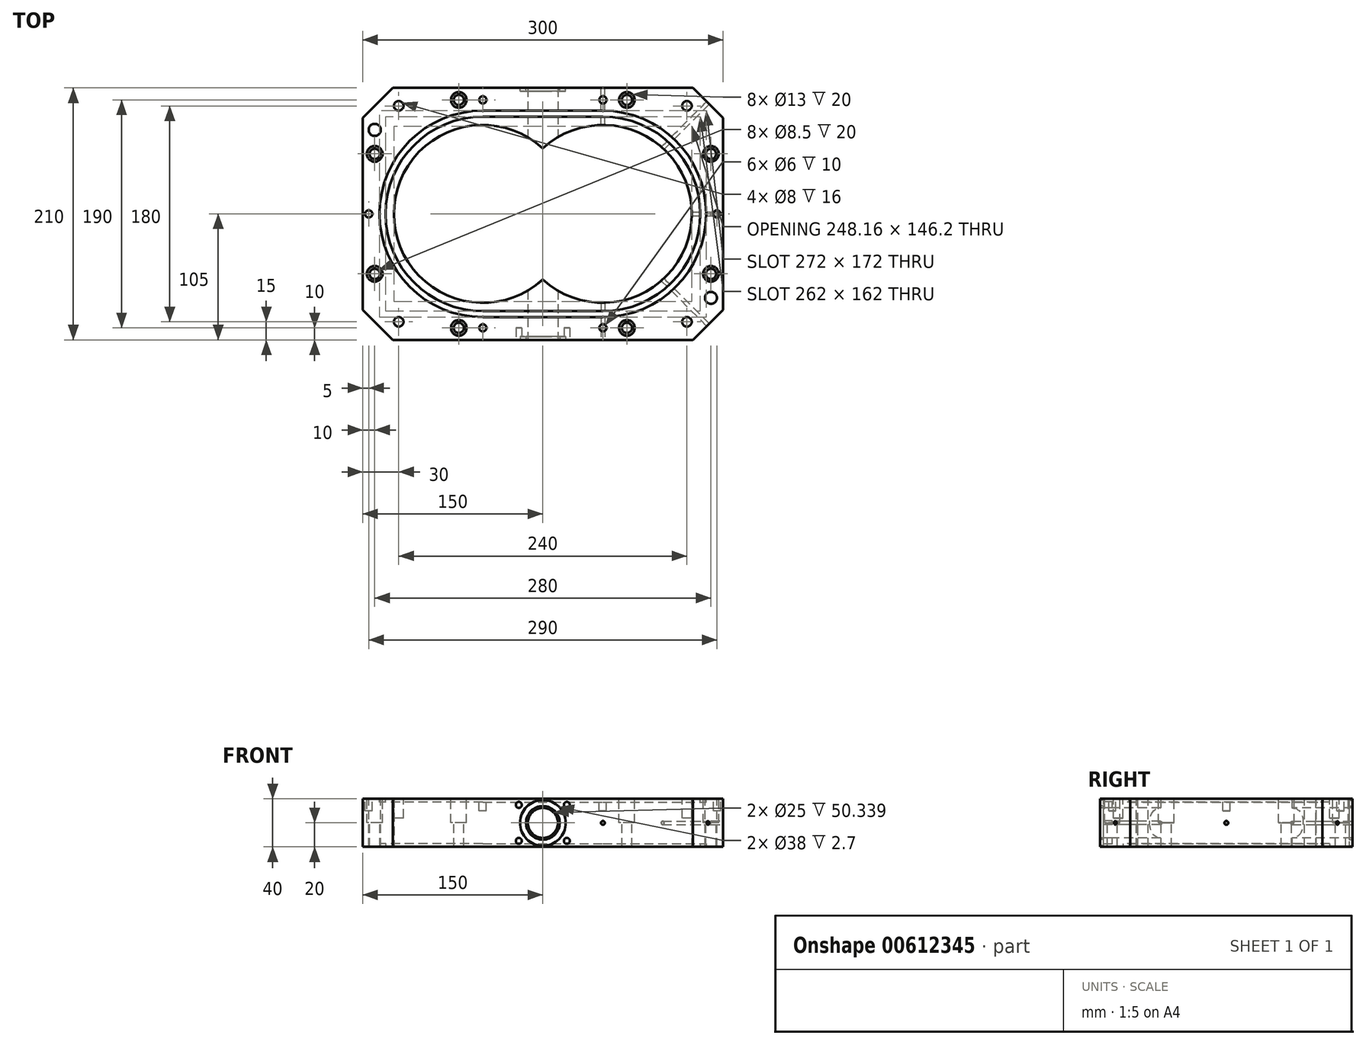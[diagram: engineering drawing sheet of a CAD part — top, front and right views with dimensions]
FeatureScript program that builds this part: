
annotation { "Feature Type Name" : "Feature", "Feature Type Description" : "" }
export const myFeature = defineFeature(function(context is Context, id is Id, definition is map)
    precondition{}
    {
        {
            var Q0;
            Q0=qCreatedBy(makeId("Top.planeOp"),FACE);
            var sketch = newSketch(context, id + "F0", { "sketchPlane" : qUnion([Q0])});
            skLineSegment(sketch, "E0.top", {"start": v(-150, 105) * mm, "end": v(150, 105) * mm});
            skLineSegment(sketch, "E0.right", {"start": v(150, -105) * mm, "end": v(150, 105) * mm});
            skArc(sketch, "E1", {"start": v(-50, 81) * mm, "mid": v(-131, 0) * mm, "end": v(-50, -81) * mm});
            skArc(sketch, "E2", {"start": v(50, -81) * mm, "mid": v(131, 0) * mm, "end": v(50, 81) * mm});
            skArc(sketch, "E3", {"start": v(-50, 86) * mm, "mid": v(-136, 0) * mm, "end": v(-50, -86) * mm});
            skArc(sketch, "E4", {"start": v(0, 54.66) * mm, "mid": v(-124.08, 0) * mm, "end": v(0, -54.66) * mm});
            skArc(sketch, "E5", {"start": v(50, -86) * mm, "mid": v(136, 0) * mm, "end": v(50, 86) * mm});
            skArc(sketch, "E6", {"start": v(0, -54.66) * mm, "mid": v(124.08, 0) * mm, "end": v(0, 54.66) * mm});
            skLineSegment(sketch, "E7", {"start": v(-50, -81) * mm, "end": v(50, -81) * mm});
            skLineSegment(sketch, "E8", {"start": v(-50, 81) * mm, "end": v(50, 81) * mm});
            skLineSegment(sketch, "E9", {"start": v(-50, 86) * mm, "end": v(50, 86) * mm});
            skLineSegment(sketch, "E10", {"start": v(50, -86) * mm, "end": v(-50, -86) * mm});
            skLineSegment(sketch, "E11", {"start": v(-150, 105) * mm, "end": v(-150, -105) * mm});
            skLineSegment(sketch, "E12", {"start": v(-150, -105) * mm, "end": v(150, -105) * mm});
            skSolve(sketch);
        }
        {
            var Q0;
            Q0=makeQuery(id+"F0.imprint","IMPRINT",FACE,{"disambiguationData":[TD([[makeQuery(id+"F0.imprint","IMPRINT",EDGE,{"derivedFrom":sQuery(id+"F0.wireOp",EDGE,"E0.top")}),-1.0]])]});
            var Q1;
            Q1=makeQuery(id+"F0.imprint","IMPRINT",FACE,{"disambiguationData":[TD([[makeQuery(id+"F0.imprint","IMPRINT",EDGE,{"derivedFrom":sQuery(id+"F0.wireOp",EDGE,"E1")}),-1.0]])]});
            var Q2;
            Q2=makeQuery(id+"F0.imprint","IMPRINT",FACE,{"disambiguationData":[TD([[makeQuery(id+"F0.imprint","IMPRINT",EDGE,{"derivedFrom":sQuery(id+"F0.wireOp",EDGE,"E1")}),1.0]])]});
            extrude(context, id + "F1", {"entities" : qUnion([Q0, Q1, Q2]), "depth" : 20 * mm, "offsetDistance" : 25 * mm, "hasSecondDirection" : true, "secondDirectionOppositeDirection" : true, "secondDirectionDepth" : 20 * mm});
        }
        {
            var Q0;
            Q0=qCreatedBy(makeId("Front.planeOp"),FACE);
            var sketch = newSketch(context, id + "F2", { "sketchPlane" : qUnion([Q0])});
            skCircle(sketch, "E13", {"center": v(0, 0) * mm, "radius": 12.5 * mm});
            skSolve(sketch);
        }
        {
            var Q0;
            Q0=makeQuery(id+"F2.imprint","IMPRINT",FACE,{"disambiguationData":[TD([[makeQuery(id+"F2.imprint","IMPRINT",EDGE,{"derivedFrom":sQuery(id+"F2.wireOp",EDGE,"E13")}),1.0]])]});
            extrude(context, id + "F3", {"entities" : qUnion([Q0]), "operationType" : NewBodyOperationType.REMOVE, "oppositeDirection" : true, "depth" : 105 * mm, "offsetDistance" : 25 * mm, "hasSecondDirection" : true, "secondDirectionOppositeDirection" : false, "secondDirectionDepth" : 105 * mm});
        }
        {
            var Q0;
            Q0=makeQuery(id+"F1.opExtrude","SWEPT_FACE",FACE,{"disambiguationData":[OSD([sQuery(id+"F0.wireOp",EDGE,"E12")])]});
            var sketch = newSketch(context, id + "F4", { "sketchPlane" : qUnion([Q0])});
            skCircle(sketch, "E14", {"center": v(0, 0) * mm, "radius": 19 * mm});
            skCircle(sketch, "E15", {"center": v(0, 0) * mm, "radius": 14 * mm});
            skCircle(sketch, "E16", {"center": v(50, 0) * mm, "radius": 1.59 * mm});
            skCircle(sketch, "E17", {"center": v(50, 0) * mm, "radius": 1.5 * mm});
            skCircle(sketch, "E18", {"center": v(-20, 15) * mm, "radius": 2.5 * mm});
            skCircle(sketch, "E19", {"center": v(-20, -15) * mm, "radius": 2.5 * mm});
            skCircle(sketch, "E20", {"center": v(20, -15) * mm, "radius": 2.5 * mm});
            skCircle(sketch, "E21", {"center": v(20, 15) * mm, "radius": 2.5 * mm});
            skSolve(sketch);
        }
        {
            var Q0;
            Q0=makeQuery(id+"F4.imprint","IMPRINT",FACE,{"disambiguationData":[TD([[makeQuery(id+"F4.imprint","IMPRINT",EDGE,{"derivedFrom":sQuery(id+"F4.wireOp",EDGE,"E14")}),1.0]])]});
            extrude(context, id + "F5", {"entities" : qUnion([Q0]), "operationType" : NewBodyOperationType.REMOVE, "oppositeDirection" : true, "depth" : 2.7 * mm, "offsetDistance" : 25 * mm});
        }
        {
            var Q0;
            Q0=makeQuery(id+"F1.opExtrude","SWEPT_FACE",FACE,{"disambiguationData":[OSD([sQuery(id+"F0.wireOp",EDGE,"E0.top")])]});
            var sketch = newSketch(context, id + "F6", { "sketchPlane" : qUnion([Q0])});
            skCircle(sketch, "E22", {"center": v(0, 0) * mm, "radius": 19 * mm});
            skCircle(sketch, "E23", {"center": v(0, 0) * mm, "radius": 14 * mm});
            skCircle(sketch, "E24", {"center": v(-50, 0) * mm, "radius": 1.59 * mm});
            skCircle(sketch, "E25", {"center": v(-50, 0) * mm, "radius": 1.5 * mm});
            skSolve(sketch);
        }
        {
            var Q0;
            Q0=makeQuery(id+"F6.imprint","IMPRINT",FACE,{"disambiguationData":[TD([[makeQuery(id+"F6.imprint","IMPRINT",EDGE,{"derivedFrom":sQuery(id+"F6.wireOp",EDGE,"E22")}),1.0]])]});
            extrude(context, id + "F7", {"entities" : qUnion([Q0]), "operationType" : NewBodyOperationType.REMOVE, "oppositeDirection" : true, "depth" : 2.7 * mm, "offsetDistance" : 25 * mm});
        }
        {
            var Q0;
            Q0=makeQuery(id+"F1.opExtrude","CAP_FACE",FACE,{"disambiguationData":[OSD([sQuery(id+"F0.wireOp",EDGE,"E0.top"),sQuery(id+"F0.wireOp",EDGE,"E0.right"),sQuery(id+"F0.wireOp",EDGE,"E3"),sQuery(id+"F0.wireOp",EDGE,"E5"),sQuery(id+"F0.wireOp",EDGE,"E9"),sQuery(id+"F0.wireOp",EDGE,"E10"),sQuery(id+"F0.wireOp",EDGE,"E11"),sQuery(id+"F0.wireOp",EDGE,"E12")])],"isStart":false});
            var sketch = newSketch(context, id + "F8", { "sketchPlane" : qUnion([Q0])});
            skCircle(sketch, "E26", {"center": v(-70, 95) * mm, "radius": 6.5 * mm});
            skCircle(sketch, "E27", {"center": v(70, 95) * mm, "radius": 6.5 * mm});
            skCircle(sketch, "E28", {"center": v(70, -95) * mm, "radius": 6.5 * mm});
            skCircle(sketch, "E29", {"center": v(-70, -95) * mm, "radius": 6.5 * mm});
            skCircle(sketch, "E30", {"center": v(-140, -50) * mm, "radius": 6.5 * mm});
            skCircle(sketch, "E31", {"center": v(-140, 50) * mm, "radius": 6.5 * mm});
            skCircle(sketch, "E32", {"center": v(140, 50) * mm, "radius": 6.5 * mm});
            skCircle(sketch, "E33", {"center": v(140, -50) * mm, "radius": 6.5 * mm});
            skCircle(sketch, "E34", {"center": v(-140, 70) * mm, "radius": 5 * mm});
            skCircle(sketch, "E35", {"center": v(140, -70) * mm, "radius": 5 * mm});
            skCircle(sketch, "E36", {"center": v(-145, 0) * mm, "radius": 3 * mm});
            skCircle(sketch, "E37", {"center": v(145, 0) * mm, "radius": 3 * mm});
            skCircle(sketch, "E38", {"center": v(50, -95) * mm, "radius": 3 * mm});
            skCircle(sketch, "E39", {"center": v(-50, -95) * mm, "radius": 3 * mm});
            skCircle(sketch, "E40", {"center": v(-50, 95) * mm, "radius": 3 * mm});
            skCircle(sketch, "E41", {"center": v(50, 95) * mm, "radius": 3 * mm});
            skCircle(sketch, "E42", {"center": v(-120, 90) * mm, "radius": 4 * mm});
            skCircle(sketch, "E43", {"center": v(-120, -90) * mm, "radius": 4 * mm});
            skCircle(sketch, "E44", {"center": v(120, -90) * mm, "radius": 4 * mm});
            skCircle(sketch, "E45", {"center": v(120, 90) * mm, "radius": 4 * mm});
            skCircle(sketch, "E46", {"center": v(-70, 95) * mm, "radius": 4.25 * mm});
            skCircle(sketch, "E47", {"center": v(70, 95) * mm, "radius": 4.25 * mm});
            skCircle(sketch, "E48", {"center": v(140, 50) * mm, "radius": 4.25 * mm});
            skCircle(sketch, "E49", {"center": v(140, -50) * mm, "radius": 4.25 * mm});
            skCircle(sketch, "E50", {"center": v(70, -95) * mm, "radius": 4.25 * mm});
            skCircle(sketch, "E51", {"center": v(-70, -95) * mm, "radius": 4.25 * mm});
            skCircle(sketch, "E52", {"center": v(-140, -50) * mm, "radius": 4.25 * mm});
            skCircle(sketch, "E53", {"center": v(-140, 50) * mm, "radius": 4.25 * mm});
            skSolve(sketch);
        }
        {
            var Q0;
            Q0=makeQuery(id+"F8.imprint","IMPRINT",FACE,{"disambiguationData":[TD([[makeQuery(id+"F8.imprint","IMPRINT",EDGE,{"derivedFrom":sQuery(id+"F8.wireOp",EDGE,"E32")}),1.0]])]});
            var Q1;
            Q1=makeQuery(id+"F8.imprint","IMPRINT",FACE,{"disambiguationData":[TD([[makeQuery(id+"F8.imprint","IMPRINT",EDGE,{"derivedFrom":sQuery(id+"F8.wireOp",EDGE,"E33")}),1.0]])]});
            var Q2;
            Q2=makeQuery(id+"F8.imprint","IMPRINT",FACE,{"disambiguationData":[TD([[makeQuery(id+"F8.imprint","IMPRINT",EDGE,{"derivedFrom":sQuery(id+"F8.wireOp",EDGE,"E28")}),1.0]])]});
            var Q3;
            Q3=makeQuery(id+"F8.imprint","IMPRINT",FACE,{"disambiguationData":[TD([[makeQuery(id+"F8.imprint","IMPRINT",EDGE,{"derivedFrom":sQuery(id+"F8.wireOp",EDGE,"E29")}),1.0]])]});
            var Q4;
            Q4=makeQuery(id+"F8.imprint","IMPRINT",FACE,{"disambiguationData":[TD([[makeQuery(id+"F8.imprint","IMPRINT",EDGE,{"derivedFrom":sQuery(id+"F8.wireOp",EDGE,"E30")}),1.0]])]});
            var Q5;
            Q5=makeQuery(id+"F8.imprint","IMPRINT",FACE,{"disambiguationData":[TD([[makeQuery(id+"F8.imprint","IMPRINT",EDGE,{"derivedFrom":sQuery(id+"F8.wireOp",EDGE,"E31")}),1.0]])]});
            var Q6;
            Q6=makeQuery(id+"F8.imprint","IMPRINT",FACE,{"disambiguationData":[TD([[makeQuery(id+"F8.imprint","IMPRINT",EDGE,{"derivedFrom":sQuery(id+"F8.wireOp",EDGE,"E26")}),1.0]])]});
            var Q7;
            Q7=makeQuery(id+"F8.imprint","IMPRINT",FACE,{"disambiguationData":[TD([[makeQuery(id+"F8.imprint","IMPRINT",EDGE,{"derivedFrom":sQuery(id+"F8.wireOp",EDGE,"E27")}),1.0]])]});
            extrude(context, id + "F9", {"entities" : qUnion([Q0, Q1, Q2, Q3, Q4, Q5, Q6, Q7]), "operationType" : NewBodyOperationType.REMOVE, "oppositeDirection" : true, "depth" : 20 * mm, "offsetDistance" : 25 * mm});
        }
        {
            var Q0;
            Q0=makeQuery(id+"F8.imprint","IMPRINT",FACE,{"disambiguationData":[TD([[makeQuery(id+"F8.imprint","IMPRINT",EDGE,{"derivedFrom":sQuery(id+"F8.wireOp",EDGE,"E40")}),1.0]])]});
            var Q1;
            Q1=makeQuery(id+"F8.imprint","IMPRINT",FACE,{"disambiguationData":[TD([[makeQuery(id+"F8.imprint","IMPRINT",EDGE,{"derivedFrom":sQuery(id+"F8.wireOp",EDGE,"E36")}),1.0]])]});
            var Q2;
            Q2=makeQuery(id+"F8.imprint","IMPRINT",FACE,{"disambiguationData":[TD([[makeQuery(id+"F8.imprint","IMPRINT",EDGE,{"derivedFrom":sQuery(id+"F8.wireOp",EDGE,"E41")}),1.0]])]});
            var Q3;
            Q3=makeQuery(id+"F8.imprint","IMPRINT",FACE,{"disambiguationData":[TD([[makeQuery(id+"F8.imprint","IMPRINT",EDGE,{"derivedFrom":sQuery(id+"F8.wireOp",EDGE,"E37")}),1.0]])]});
            var Q4;
            Q4=makeQuery(id+"F8.imprint","IMPRINT",FACE,{"disambiguationData":[TD([[makeQuery(id+"F8.imprint","IMPRINT",EDGE,{"derivedFrom":sQuery(id+"F8.wireOp",EDGE,"E39")}),1.0]])]});
            var Q5;
            Q5=makeQuery(id+"F8.imprint","IMPRINT",FACE,{"disambiguationData":[TD([[makeQuery(id+"F8.imprint","IMPRINT",EDGE,{"derivedFrom":sQuery(id+"F8.wireOp",EDGE,"E38")}),1.0]])]});
            extrude(context, id + "F10", {"entities" : qUnion([Q0, Q1, Q2, Q3, Q4, Q5]), "operationType" : NewBodyOperationType.REMOVE, "oppositeDirection" : true, "depth" : 10 * mm, "offsetDistance" : 25 * mm});
        }
        {
            var Q0;
            Q0=makeQuery(id+"F8.imprint","IMPRINT",FACE,{"disambiguationData":[TD([[makeQuery(id+"F8.imprint","IMPRINT",EDGE,{"derivedFrom":sQuery(id+"F8.wireOp",EDGE,"E46")}),1.0]])]});
            var Q1;
            Q1=makeQuery(id+"F8.imprint","IMPRINT",FACE,{"disambiguationData":[TD([[makeQuery(id+"F8.imprint","IMPRINT",EDGE,{"derivedFrom":sQuery(id+"F8.wireOp",EDGE,"E53")}),1.0]])]});
            var Q2;
            Q2=makeQuery(id+"F8.imprint","IMPRINT",FACE,{"disambiguationData":[TD([[makeQuery(id+"F8.imprint","IMPRINT",EDGE,{"derivedFrom":sQuery(id+"F8.wireOp",EDGE,"E52")}),1.0]])]});
            var Q3;
            Q3=makeQuery(id+"F8.imprint","IMPRINT",FACE,{"disambiguationData":[TD([[makeQuery(id+"F8.imprint","IMPRINT",EDGE,{"derivedFrom":sQuery(id+"F8.wireOp",EDGE,"E51")}),1.0]])]});
            var Q4;
            Q4=makeQuery(id+"F8.imprint","IMPRINT",FACE,{"disambiguationData":[TD([[makeQuery(id+"F8.imprint","IMPRINT",EDGE,{"derivedFrom":sQuery(id+"F8.wireOp",EDGE,"E50")}),1.0]])]});
            var Q5;
            Q5=makeQuery(id+"F8.imprint","IMPRINT",FACE,{"disambiguationData":[TD([[makeQuery(id+"F8.imprint","IMPRINT",EDGE,{"derivedFrom":sQuery(id+"F8.wireOp",EDGE,"E49")}),1.0]])]});
            var Q6;
            Q6=makeQuery(id+"F8.imprint","IMPRINT",FACE,{"disambiguationData":[TD([[makeQuery(id+"F8.imprint","IMPRINT",EDGE,{"derivedFrom":sQuery(id+"F8.wireOp",EDGE,"E48")}),1.0]])]});
            var Q7;
            Q7=makeQuery(id+"F8.imprint","IMPRINT",FACE,{"disambiguationData":[TD([[makeQuery(id+"F8.imprint","IMPRINT",EDGE,{"derivedFrom":sQuery(id+"F8.wireOp",EDGE,"E47")}),1.0]])]});
            var Q8;
            Q8=makeQuery(id+"F8.imprint","IMPRINT",FACE,{"disambiguationData":[TD([[makeQuery(id+"F8.imprint","IMPRINT",EDGE,{"derivedFrom":sQuery(id+"F8.wireOp",EDGE,"E34")}),1.0]])]});
            var Q9;
            Q9=makeQuery(id+"F8.imprint","IMPRINT",FACE,{"disambiguationData":[TD([[makeQuery(id+"F8.imprint","IMPRINT",EDGE,{"derivedFrom":sQuery(id+"F8.wireOp",EDGE,"E35")}),1.0]])]});
            extrude(context, id + "F11", {"entities" : qUnion([Q0, Q1, Q2, Q3, Q4, Q5, Q6, Q7, Q8, Q9]), "operationType" : NewBodyOperationType.REMOVE, "oppositeDirection" : true, "depth" : 40 * mm, "offsetDistance" : 25 * mm});
        }
        {
            var Q0;
            Q0=makeQuery(id+"F8.imprint","IMPRINT",FACE,{"disambiguationData":[TD([[makeQuery(id+"F8.imprint","IMPRINT",EDGE,{"derivedFrom":sQuery(id+"F8.wireOp",EDGE,"E42")}),1.0]])]});
            var Q1;
            Q1=makeQuery(id+"F8.imprint","IMPRINT",FACE,{"disambiguationData":[TD([[makeQuery(id+"F8.imprint","IMPRINT",EDGE,{"derivedFrom":sQuery(id+"F8.wireOp",EDGE,"E43")}),1.0]])]});
            var Q2;
            Q2=makeQuery(id+"F8.imprint","IMPRINT",FACE,{"disambiguationData":[TD([[makeQuery(id+"F8.imprint","IMPRINT",EDGE,{"derivedFrom":sQuery(id+"F8.wireOp",EDGE,"E44")}),1.0]])]});
            var Q3;
            Q3=makeQuery(id+"F8.imprint","IMPRINT",FACE,{"disambiguationData":[TD([[makeQuery(id+"F8.imprint","IMPRINT",EDGE,{"derivedFrom":sQuery(id+"F8.wireOp",EDGE,"E45")}),1.0]])]});
            extrude(context, id + "F12", {"entities" : qUnion([Q0, Q1, Q2, Q3]), "operationType" : NewBodyOperationType.REMOVE, "oppositeDirection" : true, "depth" : 16 * mm, "offsetDistance" : 25 * mm});
        }
        {
            var Q0;
            Q0=makeQuery(id+"F1.opExtrude","SWEPT_EDGE",EDGE,{"disambiguationData":[OSD([sQuery(id+"F0.wireOp",EDGE,"E0.top"),sQuery(id+"F0.wireOp",EDGE,"E11")])]});
            var Q1;
            Q1=makeQuery(id+"F1.opExtrude","SWEPT_EDGE",EDGE,{"disambiguationData":[OSD([sQuery(id+"F0.wireOp",EDGE,"E11"),sQuery(id+"F0.wireOp",EDGE,"E12")])]});
            var Q2;
            Q2=makeQuery(id+"F1.opExtrude","SWEPT_EDGE",EDGE,{"disambiguationData":[OSD([sQuery(id+"F0.wireOp",EDGE,"E0.top"),sQuery(id+"F0.wireOp",EDGE,"E0.right")])]});
            var Q3;
            Q3=makeQuery(id+"F1.opExtrude","SWEPT_EDGE",EDGE,{"disambiguationData":[OSD([sQuery(id+"F0.wireOp",EDGE,"E0.right"),sQuery(id+"F0.wireOp",EDGE,"E12")])]});
            chamfer(context, id + "F13", {"entities" : qUnion([Q0, Q1, Q2, Q3]), "width" : 25 * mm, "tangentPropagation" : true});
        }
        {
            var Q0;
            Q0=makeQuery(id+"F1.opExtrude","SWEPT_FACE",FACE,{"disambiguationData":[OSD([sQuery(id+"F0.wireOp",EDGE,"E0.right")])]});
            var sketch = newSketch(context, id + "F14", { "sketchPlane" : qUnion([Q0])});
            skCircle(sketch, "E54", {"center": v(0, 0) * mm, "radius": 1.59 * mm});
            skCircle(sketch, "E55", {"center": v(0, 0) * mm, "radius": 1.5 * mm});
            skSolve(sketch);
        }
        {
            var Q0;
            Q0=makeQuery(id+"F14.imprint","IMPRINT",FACE,{"disambiguationData":[TD([[makeQuery(id+"F14.imprint","IMPRINT",EDGE,{"derivedFrom":sQuery(id+"F14.wireOp",EDGE,"E54")}),1.0]])]});
            extrude(context, id + "F15", {"entities" : qUnion([Q0]), "operationType" : NewBodyOperationType.REMOVE, "oppositeDirection" : true, "depth" : 10 * mm, "offsetDistance" : 25 * mm});
        }
        {
            var Q0;
            Q0=makeQuery(id+"F15.boolean.opBoolean","SPLIT",FACE,{"disambiguationData":[TD([makeQuery(id+"F15.opExtrude","SWEPT_FACE",FACE,{"disambiguationData":[OSD([sQuery(id+"F14.wireOp",EDGE,"E55")])]})])],"derivedFrom":makeQuery(id+"F1.opExtrude","SWEPT_FACE",FACE,{"disambiguationData":[OSD([sQuery(id+"F0.wireOp",EDGE,"E0.right")])]})});
            extrude(context, id + "F16", {"entities" : qUnion([Q0]), "operationType" : NewBodyOperationType.REMOVE, "oppositeDirection" : true, "depth" : 40 * mm, "offsetDistance" : 25 * mm});
        }
        {
            var Q0;
            Q0=makeQuery(id+"F4.imprint","IMPRINT",FACE,{"disambiguationData":[TD([[makeQuery(id+"F4.imprint","IMPRINT",EDGE,{"derivedFrom":sQuery(id+"F4.wireOp",EDGE,"E16")}),1.0]])]});
            extrude(context, id + "F17", {"entities" : qUnion([Q0]), "operationType" : NewBodyOperationType.REMOVE, "oppositeDirection" : true, "depth" : 10 * mm, "offsetDistance" : 25 * mm});
        }
        {
            var Q0;
            Q0=makeQuery(id+"F4.imprint","IMPRINT",FACE,{"disambiguationData":[TD([[makeQuery(id+"F4.imprint","IMPRINT",EDGE,{"derivedFrom":sQuery(id+"F4.wireOp",EDGE,"E17")}),1.0]])]});
            extrude(context, id + "F18", {"entities" : qUnion([Q0]), "operationType" : NewBodyOperationType.REMOVE, "oppositeDirection" : true, "depth" : 40 * mm, "offsetDistance" : 25 * mm});
        }
        {
            var Q0;
            Q0=makeQuery(id+"F6.imprint","IMPRINT",FACE,{"disambiguationData":[TD([[makeQuery(id+"F6.imprint","IMPRINT",EDGE,{"derivedFrom":sQuery(id+"F6.wireOp",EDGE,"E25")}),1.0]])]});
            extrude(context, id + "F19", {"entities" : qUnion([Q0]), "operationType" : NewBodyOperationType.REMOVE, "oppositeDirection" : true, "depth" : 40 * mm, "offsetDistance" : 25 * mm});
        }
        {
            var Q0;
            Q0=makeQuery(id+"F13.opChamfer","BLEND_FACE",FACE,{"disambiguationData":[OSD([sQuery(id+"F0.wireOp",EDGE,"E0.right"),sQuery(id+"F0.wireOp",EDGE,"E12")])]});
            var sketch = newSketch(context, id + "F20", { "sketchPlane" : qUnion([Q0])});
            skCircle(sketch, "E56", {"center": v(31.82, 0) * mm, "radius": 1.59 * mm});
            skCircle(sketch, "E57", {"center": v(31.82, 0) * mm, "radius": 1.5 * mm});
            skSolve(sketch);
        }
        {
            var Q0;
            Q0=makeQuery(id+"F20.imprint","IMPRINT",FACE,{"disambiguationData":[TD([[makeQuery(id+"F20.imprint","IMPRINT",EDGE,{"derivedFrom":sQuery(id+"F20.wireOp",EDGE,"E57")}),1.0]])]});
            extrude(context, id + "F21", {"entities" : qUnion([Q0]), "operationType" : NewBodyOperationType.REMOVE, "oppositeDirection" : true, "depth" : 70 * mm, "offsetDistance" : 25 * mm});
        }
        {
            var Q0;
            Q0=makeQuery(id+"F13.opChamfer","BLEND_FACE",FACE,{"disambiguationData":[OSD([sQuery(id+"F0.wireOp",EDGE,"E0.top"),sQuery(id+"F0.wireOp",EDGE,"E0.right")])]});
            var sketch = newSketch(context, id + "F22", { "sketchPlane" : qUnion([Q0])});
            skCircle(sketch, "E58", {"center": v(-31.82, 0) * mm, "radius": 1.59 * mm});
            skCircle(sketch, "E59", {"center": v(-31.82, 0) * mm, "radius": 1.5 * mm});
            skSolve(sketch);
        }
        {
            var Q0;
            Q0=makeQuery(id+"F22.imprint","IMPRINT",FACE,{"disambiguationData":[TD([[makeQuery(id+"F22.imprint","IMPRINT",EDGE,{"derivedFrom":sQuery(id+"F22.wireOp",EDGE,"E59")}),1.0]])]});
            extrude(context, id + "F23", {"entities" : qUnion([Q0]), "operationType" : NewBodyOperationType.REMOVE, "oppositeDirection" : true, "depth" : 70 * mm, "offsetDistance" : 25 * mm});
        }
        {
            var Q0;
            Q0=makeQuery(id+"F4.imprint","IMPRINT",FACE,{"disambiguationData":[TD([[makeQuery(id+"F4.imprint","IMPRINT",EDGE,{"derivedFrom":sQuery(id+"F4.wireOp",EDGE,"E18")}),1.0]])]});
            var Q1;
            Q1=makeQuery(id+"F4.imprint","IMPRINT",FACE,{"disambiguationData":[TD([[makeQuery(id+"F4.imprint","IMPRINT",EDGE,{"derivedFrom":sQuery(id+"F4.wireOp",EDGE,"E21")}),1.0]])]});
            var Q2;
            Q2=makeQuery(id+"F4.imprint","IMPRINT",FACE,{"disambiguationData":[TD([[makeQuery(id+"F4.imprint","IMPRINT",EDGE,{"derivedFrom":sQuery(id+"F4.wireOp",EDGE,"E20")}),1.0]])]});
            var Q3;
            Q3=makeQuery(id+"F4.imprint","IMPRINT",FACE,{"disambiguationData":[TD([[makeQuery(id+"F4.imprint","IMPRINT",EDGE,{"derivedFrom":sQuery(id+"F4.wireOp",EDGE,"E19")}),1.0]])]});
            extrude(context, id + "F24", {"entities" : qUnion([Q0, Q1, Q2, Q3]), "operationType" : NewBodyOperationType.REMOVE, "oppositeDirection" : true, "depth" : 10 * mm, "offsetDistance" : 25 * mm});
        }
        {
            var Q0;
            {var subQ0=sQuery(id+"F0.wireOp",EDGE,"E0.top");var subQ1=sQuery(id+"F0.wireOp",EDGE,"E12");var subQ2=sQuery(id+"F0.wireOp",EDGE,"E11");var subQ3=sQuery(id+"F0.wireOp",EDGE,"E0.right");var subQ4=sQuery(id+"F0.wireOp",EDGE,"E6");var subQ5=sQuery(id+"F0.wireOp",EDGE,"E4");Q0=makeQuery(id+"F9.boolean.opBoolean","SPLIT",FACE,{"disambiguationData":[TD([makeQuery(id+"F1.opExtrude","SWEPT_FACE",FACE,{"disambiguationData":[OSD([subQ0])]})])],"derivedFrom":makeQuery(id+"F1.opExtrude","CAP_FACE",FACE,{"disambiguationData":[OSD([subQ0,subQ3,subQ5,subQ4,subQ2,subQ1])],"isStart":false})});}
            var sketch = newSketch(context, id + "F25", { "sketchPlane" : qUnion([Q0])});
            skArc(sketch, "E60", {"start": v(50, -86) * mm, "mid": v(136, 0) * mm, "end": v(50, 86) * mm});
            skArc(sketch, "E61", {"start": v(50, -81) * mm, "mid": v(131, 0) * mm, "end": v(50, 81) * mm});
            skArc(sketch, "E62", {"start": v(-50, 86) * mm, "mid": v(-136, 0) * mm, "end": v(-50, -86) * mm});
            skArc(sketch, "E63", {"start": v(-50, 81) * mm, "mid": v(-131, 0) * mm, "end": v(-50, -81) * mm});
            skLineSegment(sketch, "E64", {"start": v(-50, 86) * mm, "end": v(50, 86) * mm});
            skLineSegment(sketch, "E65", {"start": v(50, 81) * mm, "end": v(-50, 81) * mm});
            skLineSegment(sketch, "E66", {"start": v(-50, -81) * mm, "end": v(50, -81) * mm});
            skLineSegment(sketch, "E67", {"start": v(50, -86) * mm, "end": v(-50, -86) * mm});
            skSolve(sketch);
        }
        {
            var Q0;
            Q0=makeQuery(id+"F25.imprint","IMPRINT",FACE,{"disambiguationData":[TD([[makeQuery(id+"F25.imprint","IMPRINT",EDGE,{"derivedFrom":sQuery(id+"F25.wireOp",EDGE,"E60")}),1.0]])]});
            extrude(context, id + "F26", {"entities" : qUnion([Q0]), "operationType" : NewBodyOperationType.REMOVE, "oppositeDirection" : true, "depth" : 2.7 * mm, "offsetDistance" : 25 * mm});
        }
        {
            var Q0;
            Q0=makeQuery(id+"F1.opExtrude","CAP_FACE",FACE,{"disambiguationData":[OSD([sQuery(id+"F0.wireOp",EDGE,"E0.top"),sQuery(id+"F0.wireOp",EDGE,"E0.right"),sQuery(id+"F0.wireOp",EDGE,"E4"),sQuery(id+"F0.wireOp",EDGE,"E6"),sQuery(id+"F0.wireOp",EDGE,"E11"),sQuery(id+"F0.wireOp",EDGE,"E12")])],"isStart":true});
            var sketch = newSketch(context, id + "F27", { "sketchPlane" : qUnion([Q0])});
            skArc(sketch, "E68", {"start": v(-50, 86) * mm, "mid": v(-136, 0) * mm, "end": v(-50, -86) * mm});
            skArc(sketch, "E69", {"start": v(-50, 81) * mm, "mid": v(-131, 0) * mm, "end": v(-50, -81) * mm});
            skArc(sketch, "E70", {"start": v(50, -86) * mm, "mid": v(136, 0) * mm, "end": v(50, 86) * mm});
            skArc(sketch, "E71", {"start": v(50, -81) * mm, "mid": v(131, 0) * mm, "end": v(50, 81) * mm});
            skLineSegment(sketch, "E72", {"start": v(-50, 81) * mm, "end": v(50, 81) * mm});
            skLineSegment(sketch, "E73", {"start": v(50, 86) * mm, "end": v(-50, 86) * mm});
            skLineSegment(sketch, "E74", {"start": v(-50, -81) * mm, "end": v(50, -81) * mm});
            skLineSegment(sketch, "E75", {"start": v(50, -86) * mm, "end": v(-50, -86) * mm});
            skSolve(sketch);
        }
        {
            var Q0;
            Q0=makeQuery(id+"F27.imprint","IMPRINT",FACE,{"disambiguationData":[TD([[makeQuery(id+"F27.imprint","IMPRINT",EDGE,{"derivedFrom":sQuery(id+"F27.wireOp",EDGE,"E68")}),1.0]])]});
            extrude(context, id + "F28", {"entities" : qUnion([Q0]), "operationType" : NewBodyOperationType.REMOVE, "oppositeDirection" : true, "depth" : 2.7 * mm, "offsetDistance" : 25 * mm});
        }
    });
